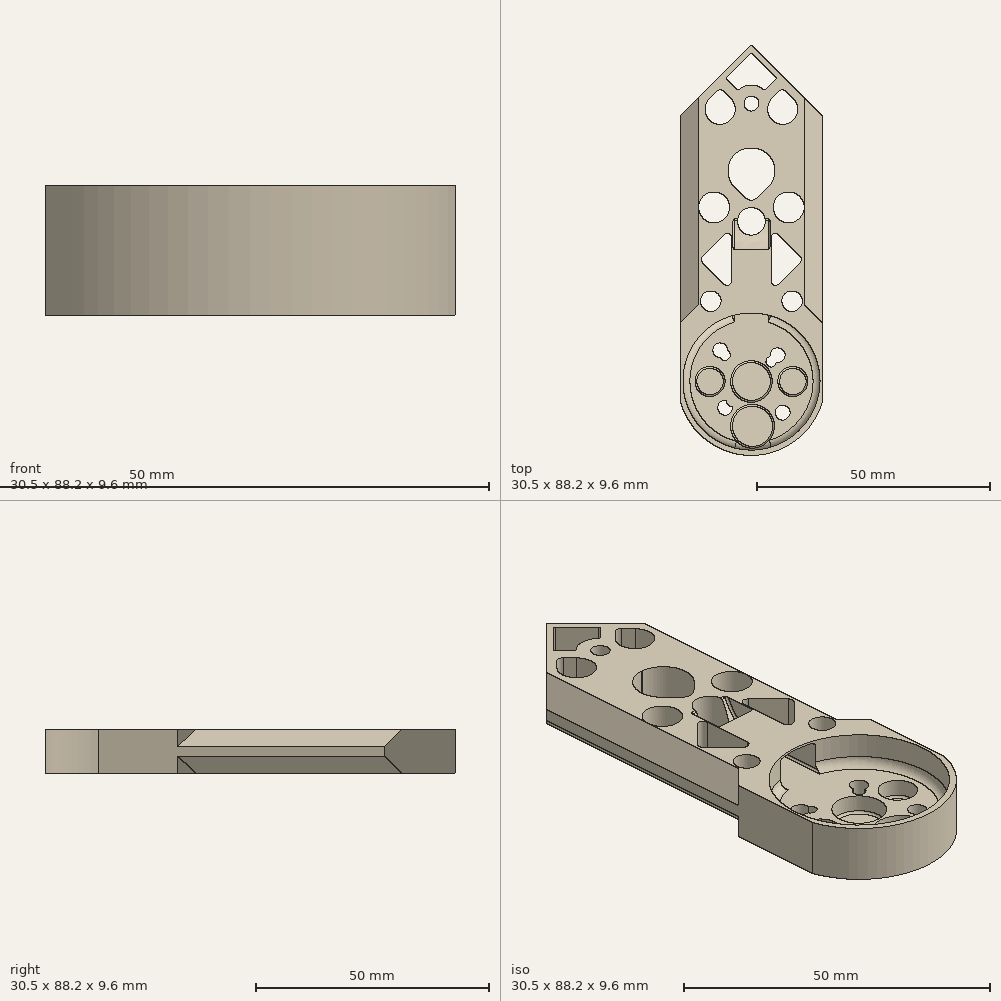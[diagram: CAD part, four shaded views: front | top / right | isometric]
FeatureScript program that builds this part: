
annotation { "Feature Type Name" : "Feature", "Feature Type Description" : "" }
export const myFeature = defineFeature(function(context is Context, id is Id, definition is map)
    precondition{}
    {
        {
            var Q0;
            Q0=qCreatedBy(makeId("Top.planeOp"),FACE);
            var sketch = newSketch(context, id + "F0", { "sketchPlane" : qUnion([Q0])});
            skLineSegment(sketch, "E0", {"start": v(0, 0) * mm, "end": v(-10, 0) * mm});
            skLineSegment(sketch, "E1", {"start": v(-7.84, 7.84) * mm, "end": v(0, 0) * mm});
            skLineSegment(sketch, "E2", {"start": v(-6.78, -6.78) * mm, "end": v(0, 0) * mm});
            skLineSegment(sketch, "E3", {"start": v(0, 0) * mm, "end": v(-5.66, -5.66) * mm});
            skCircle(sketch, "E4", {"center": v(-5.66, -5.66) * mm, "radius": 1.59 * mm});
            skLineSegment(sketch, "E5", {"start": v(0, 0) * mm, "end": v(-6.72, 6.72) * mm});
            skCircle(sketch, "E6", {"center": v(-6.72, 6.72) * mm, "radius": 1.59 * mm});
            skLineSegment(sketch, "E7", {"start": v(0, 0) * mm, "end": v(-5.66, 5.66) * mm});
            skCircle(sketch, "E8", {"center": v(-5.66, 5.66) * mm, "radius": 1.13 * mm});
            skLineSegment(sketch, "E9.MirrorCS", {"start": v(7.84, -7.84) * mm, "end": v(0, 0) * mm});
            skLineSegment(sketch, "E10.MirrorCS", {"start": v(0, 0) * mm, "end": v(5.66, -5.66) * mm});
            skCircle(sketch, "E11.MirrorC", {"center": v(6.72, -6.72) * mm, "radius": 1.59 * mm});
            skCircle(sketch, "E12.MirrorC", {"center": v(5.66, -5.66) * mm, "radius": 1.13 * mm});
            skLineSegment(sketch, "E13.MirrorCS", {"start": v(0, 0) * mm, "end": v(6.72, -6.72) * mm});
            skCircle(sketch, "E14.MirrorC", {"center": v(5.66, 5.66) * mm, "radius": 1.59 * mm});
            skLineSegment(sketch, "E15.MirrorCS", {"start": v(0, 0) * mm, "end": v(5.66, 5.66) * mm});
            skLineSegment(sketch, "E16.MirrorCS", {"start": v(6.78, 6.78) * mm, "end": v(0, 0) * mm});
            skPoint(sketch, "E17.MirrorCS.start.orphan", {"position": v(0, 10) * mm});
            skPoint(sketch, "E18.orphan", {"position": v(10, 10) * mm});
            skPoint(sketch, "E19.orphan", {"position": v(10, -10) * mm});
            skPoint(sketch, "E20.orphan", {"position": v(-10, 10) * mm});
            skPoint(sketch, "E21.orphan", {"position": v(-10, -10) * mm});
            skCircle(sketch, "E22", {"center": v(-4.24, -4.24) * mm, "radius": 1.13 * mm});
            skCircle(sketch, "E23", {"center": v(4.24, 4.24) * mm, "radius": 1.13 * mm});
            skSolve(sketch);
        }
        {
            var Q0;
            Q0=qCreatedBy(makeId("Front.planeOp"),FACE);
            var sketch = newSketch(context, id + "F1", { "sketchPlane" : qUnion([Q0])});
            skLineSegment(sketch, "E24", {"start": v(0, 0) * mm, "end": v(11.35, 0) * mm});
            skLineSegment(sketch, "E25", {"start": v(-11.35, 0) * mm, "end": v(0, 0) * mm});
            skLineSegment(sketch, "E26", {"start": v(0, 0) * mm, "end": v(0, 3.8) * mm});
            skLineSegment(sketch, "E27", {"start": v(0, 3.8) * mm, "end": v(15.25, 3.8) * mm});
            skLineSegment(sketch, "E28", {"start": v(-15.25, 3.8) * mm, "end": v(0, 3.8) * mm});
            skPoint(sketch, "E29.orphan", {"position": v(15.25, 0) * mm});
            skPoint(sketch, "E30.orphan", {"position": v(-15.25, 0) * mm});
            skLineSegment(sketch, "E31", {"start": v(-15.25, 3.8) * mm, "end": v(-11.35, 0) * mm});
            skLineSegment(sketch, "E32", {"start": v(15.25, 3.8) * mm, "end": v(11.35, 0) * mm});
            skLineSegment(sketch, "E33", {"start": v(15.25, 3.8) * mm, "end": v(15.25, 5.8) * mm});
            skLineSegment(sketch, "E34", {"start": v(15.25, 5.8) * mm, "end": v(11.35, 9.6) * mm});
            skLineSegment(sketch, "E35", {"start": v(11.35, 9.6) * mm, "end": v(0, 9.6) * mm});
            skLineSegment(sketch, "E36.MirrorCS", {"start": v(-11.35, 9.6) * mm, "end": v(0, 9.6) * mm});
            skLineSegment(sketch, "E37.MirrorCS", {"start": v(-15.25, 5.8) * mm, "end": v(-11.35, 9.6) * mm});
            skLineSegment(sketch, "E38.MirrorCS", {"start": v(-15.25, 3.8) * mm, "end": v(-15.25, 5.8) * mm});
            skSolve(sketch);
        }
        {
            var Q0;
            Q0=qSketchRegion(id+"F1",true);
            extrude(context, id + "F2", {"entities" : qUnion([Q0]), "depth" : 16.3 * mm, "hasSecondDirection" : true, "secondDirectionOppositeDirection" : true, "secondDirectionDepth" : 72.3 * mm});
        }
        {
            var Q0;
            Q0=qCreatedBy(makeId("Top.planeOp"),FACE);
            cPlane(context, id + "F3", {"entities" : qUnion([Q0]), "cplaneType" : CPlaneType.OFFSET, "offset" : 16 * mm, "width" : 150 * mm, "height" : 150 * mm});
        }
        {
            var Q0;
            Q0=makeQuery(id+"F2.opExtrude","SWEPT_FACE",FACE,{"disambiguationData":[OSD([sQuery(id+"F1.wireOp",EDGE,"E35"),sQuery(id+"F1.wireOp",EDGE,"E36.MirrorCS")])]});
            var sketch = newSketch(context, id + "F4", { "sketchPlane" : qUnion([Q0])});
            skCircle(sketch, "E39", {"center": v(0, 0) * mm, "radius": 14.75 * mm});
            skLineSegment(sketch, "E40", {"start": v(14.75, 0) * mm, "end": v(-14.75, 0) * mm});
            skSolve(sketch);
        }
        {
            var Q0;
            {var subQ0=sQuery(id+"F4.wireOp",EDGE,"E39");var subQ1=makeQuery(id+"F2.opExtrude","SWEPT_EDGE",EDGE,{"disambiguationData":[OSD([sQuery(id+"F1.wireOp",EDGE,"E34"),sQuery(id+"F1.wireOp",EDGE,"E35")])]});var subQ2=makeQuery(id+"F4.imprint","INTERSECT",VERTEX,{"disambiguationData":[OD(0.0)],"derivedFrom":[subQ1,subQ0]});Q0=makeQuery(id+"F4.imprint","IMPRINT",FACE,{"disambiguationData":[TD([[makeQuery(id+"F4.imprint","IMPRINT",EDGE,{"disambiguationData":[TD([[subQ2,-1.0]])],"derivedFrom":subQ0}),1.0]])]});}
            var Q1;
            {var subQ0=sQuery(id+"F4.wireOp",EDGE,"E39");var subQ1=makeQuery(id+"F2.opExtrude","SWEPT_EDGE",EDGE,{"disambiguationData":[OSD([sQuery(id+"F1.wireOp",EDGE,"E36.MirrorCS"),sQuery(id+"F1.wireOp",EDGE,"E37.MirrorCS")])]});var subQ2=makeQuery(id+"F4.imprint","INTERSECT",VERTEX,{"disambiguationData":[OD(1.0)],"derivedFrom":[subQ1,subQ0]});Q1=makeQuery(id+"F4.imprint","IMPRINT",FACE,{"disambiguationData":[TD([[makeQuery(id+"F4.imprint","IMPRINT",EDGE,{"disambiguationData":[TD([[subQ2,-1.0]])],"derivedFrom":subQ0}),1.0]])]});}
            var Q2;
            {var subQ0=sQuery(id+"F4.wireOp",EDGE,"E40");var subQ1=sQuery(id+"F4.wireOp",EDGE,"E39");var subQ2=makeQuery(id+"F4.imprint","INTERSECT",VERTEX,{"disambiguationData":[OD(1.0)],"derivedFrom":[subQ1,subQ0]});Q2=makeQuery(id+"F4.imprint","IMPRINT",FACE,{"disambiguationData":[TD([[makeQuery(id+"F4.imprint","IMPRINT",EDGE,{"disambiguationData":[TD([[subQ2,-1.0]])],"derivedFrom":subQ1}),1.0]])]});}
            var Q3;
            {var subQ0=sQuery(id+"F4.wireOp",EDGE,"E40");var subQ1=sQuery(id+"F4.wireOp",EDGE,"E39");var subQ2=makeQuery(id+"F4.imprint","INTERSECT",VERTEX,{"disambiguationData":[OD(1.0)],"derivedFrom":[subQ1,subQ0]});Q3=makeQuery(id+"F4.imprint","IMPRINT",FACE,{"disambiguationData":[TD([[makeQuery(id+"F4.imprint","IMPRINT",EDGE,{"disambiguationData":[TD([[subQ2,1.0]])],"derivedFrom":subQ1}),1.0]])]});}
            var Q4;
            {var subQ0=sQuery(id+"F4.wireOp",EDGE,"E40");var subQ1=sQuery(id+"F4.wireOp",EDGE,"E39");var subQ2=makeQuery(id+"F4.imprint","INTERSECT",VERTEX,{"disambiguationData":[OD(0.0)],"derivedFrom":[subQ1,subQ0]});Q4=makeQuery(id+"F4.imprint","IMPRINT",FACE,{"disambiguationData":[TD([[makeQuery(id+"F4.imprint","IMPRINT",EDGE,{"disambiguationData":[TD([[subQ2,-1.0]])],"derivedFrom":subQ1}),1.0]])]});}
            var Q5;
            {var subQ0=sQuery(id+"F4.wireOp",EDGE,"E40");var subQ1=sQuery(id+"F4.wireOp",EDGE,"E39");var subQ2=makeQuery(id+"F4.imprint","INTERSECT",VERTEX,{"disambiguationData":[OD(0.0)],"derivedFrom":[subQ1,subQ0]});Q5=makeQuery(id+"F4.imprint","IMPRINT",FACE,{"disambiguationData":[TD([[makeQuery(id+"F4.imprint","IMPRINT",EDGE,{"disambiguationData":[TD([[subQ2,1.0]])],"derivedFrom":subQ1}),1.0]])]});}
            extrude(context, id + "F5", {"entities" : qUnion([Q0, Q1, Q2, Q3, Q4, Q5]), "operationType" : NewBodyOperationType.REMOVE, "oppositeDirection" : true, "depth" : 5.6 * mm});
        }
        {
            var Q0;
            {var subQ5=sQuery(id+"F0.wireOp",EDGE,"E1");Q0=makeQuery(id+"F0.imprint","IMPRINT",FACE,{"disambiguationData":[TD([[makeQuery(id+"F0.imprint","IMPRINT",EDGE,{"derivedFrom":subQ5}),-1.0]])]});}
            var Q1;
            {var subQ3=sQuery(id+"F0.wireOp",EDGE,"E1");Q1=makeQuery(id+"F0.imprint","IMPRINT",FACE,{"disambiguationData":[TD([[makeQuery(id+"F0.imprint","IMPRINT",EDGE,{"derivedFrom":subQ3}),1.0]])]});}
            var Q2;
            {var subQ5=sQuery(id+"F0.wireOp",EDGE,"E2");Q2=makeQuery(id+"F0.imprint","IMPRINT",FACE,{"disambiguationData":[TD([[makeQuery(id+"F0.imprint","IMPRINT",EDGE,{"derivedFrom":subQ5}),1.0]])]});}
            var Q3;
            {var subQ5=sQuery(id+"F0.wireOp",EDGE,"E2");Q3=makeQuery(id+"F0.imprint","IMPRINT",FACE,{"disambiguationData":[TD([[makeQuery(id+"F0.imprint","IMPRINT",EDGE,{"derivedFrom":subQ5}),-1.0]])]});}
            var Q4;
            {var subQ0=sQuery(id+"F0.wireOp",EDGE,"E22");var subQ3=sQuery(id+"F0.wireOp",EDGE,"E3");var subQ4=makeQuery(id+"F0.imprint","INTERSECT",VERTEX,{"disambiguationData":[OD(0.0)],"derivedFrom":[subQ3,subQ0]});Q4=makeQuery(id+"F0.imprint","IMPRINT",FACE,{"disambiguationData":[TD([[makeQuery(id+"F0.imprint","IMPRINT",EDGE,{"disambiguationData":[TD([[subQ4,-1.0]])],"derivedFrom":subQ3}),1.0]])]});}
            var Q5;
            {var subQ0=sQuery(id+"F0.wireOp",EDGE,"E22");var subQ3=sQuery(id+"F0.wireOp",EDGE,"E3");var subQ4=makeQuery(id+"F0.imprint","INTERSECT",VERTEX,{"disambiguationData":[OD(0.0)],"derivedFrom":[subQ3,subQ0]});Q5=makeQuery(id+"F0.imprint","IMPRINT",FACE,{"disambiguationData":[TD([[makeQuery(id+"F0.imprint","IMPRINT",EDGE,{"disambiguationData":[TD([[subQ4,-1.0]])],"derivedFrom":subQ3}),-1.0]])]});}
            var Q6;
            {var subQ1=sQuery(id+"F0.wireOp",EDGE,"E6");var subQ3=sQuery(id+"F0.wireOp",EDGE,"E8");var subQ5=makeQuery(id+"F0.imprint","INTERSECT",VERTEX,{"disambiguationData":[OD(0.0)],"derivedFrom":[subQ1,subQ3]});Q6=makeQuery(id+"F0.imprint","IMPRINT",FACE,{"disambiguationData":[TD([[makeQuery(id+"F0.imprint","IMPRINT",EDGE,{"disambiguationData":[TD([[subQ5,-1.0]])],"derivedFrom":subQ1}),-1.0]])]});}
            var Q7;
            {var subQ1=sQuery(id+"F0.wireOp",EDGE,"E6");var subQ3=sQuery(id+"F0.wireOp",EDGE,"E8");var subQ5=makeQuery(id+"F0.imprint","INTERSECT",VERTEX,{"disambiguationData":[OD(1.0)],"derivedFrom":[subQ1,subQ3]});Q7=makeQuery(id+"F0.imprint","IMPRINT",FACE,{"disambiguationData":[TD([[makeQuery(id+"F0.imprint","IMPRINT",EDGE,{"disambiguationData":[TD([[subQ5,1.0]])],"derivedFrom":subQ1}),-1.0]])]});}
            var Q8;
            {var subQ3=sQuery(id+"F0.wireOp",EDGE,"E9.MirrorCS");Q8=makeQuery(id+"F0.imprint","IMPRINT",FACE,{"disambiguationData":[TD([[makeQuery(id+"F0.imprint","IMPRINT",EDGE,{"derivedFrom":subQ3}),1.0]])]});}
            var Q9;
            {var subQ3=sQuery(id+"F0.wireOp",EDGE,"E9.MirrorCS");Q9=makeQuery(id+"F0.imprint","IMPRINT",FACE,{"disambiguationData":[TD([[makeQuery(id+"F0.imprint","IMPRINT",EDGE,{"derivedFrom":subQ3}),-1.0]])]});}
            var Q10;
            {var subQ1=sQuery(id+"F0.wireOp",EDGE,"E11.MirrorC");var subQ3=sQuery(id+"F0.wireOp",EDGE,"E12.MirrorC");var subQ5=makeQuery(id+"F0.imprint","INTERSECT",VERTEX,{"disambiguationData":[OD(0.0)],"derivedFrom":[subQ1,subQ3]});Q10=makeQuery(id+"F0.imprint","IMPRINT",FACE,{"disambiguationData":[TD([[makeQuery(id+"F0.imprint","IMPRINT",EDGE,{"disambiguationData":[TD([[subQ5,-1.0]])],"derivedFrom":subQ1}),1.0]])]});}
            var Q11;
            {var subQ1=sQuery(id+"F0.wireOp",EDGE,"E11.MirrorC");var subQ3=sQuery(id+"F0.wireOp",EDGE,"E12.MirrorC");var subQ5=makeQuery(id+"F0.imprint","INTERSECT",VERTEX,{"disambiguationData":[OD(1.0)],"derivedFrom":[subQ1,subQ3]});Q11=makeQuery(id+"F0.imprint","IMPRINT",FACE,{"disambiguationData":[TD([[makeQuery(id+"F0.imprint","IMPRINT",EDGE,{"disambiguationData":[TD([[subQ5,1.0]])],"derivedFrom":subQ1}),1.0]])]});}
            var Q12;
            {var subQ0=sQuery(id+"F0.wireOp",EDGE,"E23");var subQ1=sQuery(id+"F0.wireOp",EDGE,"E14.MirrorC");var subQ2=makeQuery(id+"F0.imprint","INTERSECT",VERTEX,{"disambiguationData":[OD(1.0)],"derivedFrom":[subQ1,subQ0]});Q12=makeQuery(id+"F0.imprint","IMPRINT",FACE,{"disambiguationData":[TD([[makeQuery(id+"F0.imprint","IMPRINT",EDGE,{"disambiguationData":[TD([[subQ2,1.0]])],"derivedFrom":subQ1}),1.0]])]});}
            var Q13;
            {var subQ1=sQuery(id+"F0.wireOp",EDGE,"E16.MirrorCS");var subQ5=makeQuery(id+"F0.imprint","IMPRINT",VERTEX,{"derivedFrom":subQ1});Q13=makeQuery(id+"F0.imprint","IMPRINT",FACE,{"disambiguationData":[TD([[makeQuery(id+"F0.imprint","IMPRINT",EDGE,{"disambiguationData":[TD([[subQ5,1.0]])],"derivedFrom":subQ1}),-1.0]])]});}
            var Q14;
            {var subQ1=sQuery(id+"F0.wireOp",EDGE,"E16.MirrorCS");var subQ5=makeQuery(id+"F0.imprint","IMPRINT",VERTEX,{"derivedFrom":subQ1});Q14=makeQuery(id+"F0.imprint","IMPRINT",FACE,{"disambiguationData":[TD([[makeQuery(id+"F0.imprint","IMPRINT",EDGE,{"disambiguationData":[TD([[subQ5,1.0]])],"derivedFrom":subQ1}),1.0]])]});}
            var Q15;
            {var subQ1=sQuery(id+"F0.wireOp",EDGE,"E3");var subQ3=sQuery(id+"F0.wireOp",EDGE,"E4");var subQ5=makeQuery(id+"F0.imprint","INTERSECT",VERTEX,{"derivedFrom":[subQ1,subQ3]});Q15=makeQuery(id+"F0.imprint","IMPRINT",FACE,{"disambiguationData":[TD([[makeQuery(id+"F0.imprint","IMPRINT",EDGE,{"disambiguationData":[TD([[subQ5,-1.0]])],"derivedFrom":subQ1}),1.0]])]});}
            var Q16;
            {var subQ1=sQuery(id+"F0.wireOp",EDGE,"E3");var subQ3=sQuery(id+"F0.wireOp",EDGE,"E4");var subQ5=makeQuery(id+"F0.imprint","INTERSECT",VERTEX,{"derivedFrom":[subQ1,subQ3]});Q16=makeQuery(id+"F0.imprint","IMPRINT",FACE,{"disambiguationData":[TD([[makeQuery(id+"F0.imprint","IMPRINT",EDGE,{"disambiguationData":[TD([[subQ5,-1.0]])],"derivedFrom":subQ1}),-1.0]])]});}
            var Q17;
            {var subQ0=sQuery(id+"F0.wireOp",EDGE,"E13.MirrorCS");var subQ3=makeQuery(id+"F0.imprint","IMPRINT",VERTEX,{"derivedFrom":subQ0});Q17=makeQuery(id+"F0.imprint","IMPRINT",FACE,{"disambiguationData":[TD([[makeQuery(id+"F0.imprint","IMPRINT",EDGE,{"disambiguationData":[TD([[subQ3,1.0]])],"derivedFrom":subQ0}),1.0]])]});}
            var Q18;
            {var subQ0=sQuery(id+"F0.wireOp",EDGE,"E23");var subQ3=sQuery(id+"F0.wireOp",EDGE,"E14.MirrorC");var subQ4=makeQuery(id+"F0.imprint","INTERSECT",VERTEX,{"disambiguationData":[OD(1.0)],"derivedFrom":[subQ3,subQ0]});Q18=makeQuery(id+"F0.imprint","IMPRINT",FACE,{"disambiguationData":[TD([[makeQuery(id+"F0.imprint","IMPRINT",EDGE,{"disambiguationData":[TD([[subQ4,1.0]])],"derivedFrom":subQ3}),-1.0]])]});}
            var Q19;
            {var subQ0=sQuery(id+"F0.wireOp",EDGE,"E23");var subQ1=sQuery(id+"F0.wireOp",EDGE,"E14.MirrorC");var subQ2=makeQuery(id+"F0.imprint","INTERSECT",VERTEX,{"disambiguationData":[OD(0.0)],"derivedFrom":[subQ1,subQ0]});Q19=makeQuery(id+"F0.imprint","IMPRINT",FACE,{"disambiguationData":[TD([[makeQuery(id+"F0.imprint","IMPRINT",EDGE,{"disambiguationData":[TD([[subQ2,-1.0]])],"derivedFrom":subQ1}),1.0]])]});}
            var Q20;
            {var subQ0=sQuery(id+"F0.wireOp",EDGE,"E23");var subQ3=sQuery(id+"F0.wireOp",EDGE,"E14.MirrorC");var subQ4=makeQuery(id+"F0.imprint","INTERSECT",VERTEX,{"disambiguationData":[OD(0.0)],"derivedFrom":[subQ3,subQ0]});Q20=makeQuery(id+"F0.imprint","IMPRINT",FACE,{"disambiguationData":[TD([[makeQuery(id+"F0.imprint","IMPRINT",EDGE,{"disambiguationData":[TD([[subQ4,-1.0]])],"derivedFrom":subQ3}),-1.0]])]});}
            var Q21;
            {var subQ0=sQuery(id+"F0.wireOp",EDGE,"E13.MirrorCS");var subQ3=makeQuery(id+"F0.imprint","IMPRINT",VERTEX,{"derivedFrom":subQ0});Q21=makeQuery(id+"F0.imprint","IMPRINT",FACE,{"disambiguationData":[TD([[makeQuery(id+"F0.imprint","IMPRINT",EDGE,{"disambiguationData":[TD([[subQ3,1.0]])],"derivedFrom":subQ0}),-1.0]])]});}
            var Q22;
            {var subQ1=sQuery(id+"F0.wireOp",EDGE,"E5");var subQ5=sQuery(id+"F0.wireOp",EDGE,"E7");var subQ7=makeQuery(id+"F0.imprint","INTERSECT",VERTEX,{"derivedFrom":[subQ1,subQ5]});Q22=makeQuery(id+"F0.imprint","IMPRINT",FACE,{"disambiguationData":[TD([[makeQuery(id+"F0.imprint","IMPRINT",EDGE,{"disambiguationData":[TD([[subQ7,-1.0]])],"derivedFrom":subQ1}),1.0]])]});}
            var Q23;
            {var subQ1=sQuery(id+"F0.wireOp",EDGE,"E5");var subQ5=sQuery(id+"F0.wireOp",EDGE,"E7");var subQ7=makeQuery(id+"F0.imprint","INTERSECT",VERTEX,{"derivedFrom":[subQ1,subQ5]});Q23=makeQuery(id+"F0.imprint","IMPRINT",FACE,{"disambiguationData":[TD([[makeQuery(id+"F0.imprint","IMPRINT",EDGE,{"disambiguationData":[TD([[subQ7,-1.0]])],"derivedFrom":subQ1}),-1.0]])]});}
            extrude(context, id + "F6", {"entities" : qUnion([Q0, Q1, Q2, Q3, Q4, Q5, Q6, Q7, Q8, Q9, Q10, Q11, Q12, Q13, Q14, Q15, Q16, Q17, Q18, Q19, Q20, Q21, Q22, Q23]), "operationType" : NewBodyOperationType.REMOVE, "endBound" : BoundingType.THROUGH_ALL, "depth" : 5 * mm});
        }
        {
            var Q0;
            Q0=qCreatedBy(makeId("Top.planeOp"),FACE);
            var sketch = newSketch(context, id + "F7", { "sketchPlane" : qUnion([Q0])});
            skCircle(sketch, "E41", {"center": v(0, 0) * mm, "radius": 14.75 * mm});
            skArc(sketch, "E42", {"start": v(15.25, 4.5) * mm, "mid": v(0, 15.9) * mm, "end": v(-15.25, 4.5) * mm});
            skLineSegment(sketch, "E43", {"start": v(0, 0) * mm, "end": v(15.25, 0) * mm});
            skLineSegment(sketch, "E44", {"start": v(15.25, 0) * mm, "end": v(15.25, 4.5) * mm});
            skLineSegment(sketch, "E45.MirrorCS", {"start": v(15.25, 0) * mm, "end": v(15.25, -4.5) * mm});
            skLineSegment(sketch, "E46.MirrorCS", {"start": v(-15.25, 0) * mm, "end": v(-15.25, 4.5) * mm});
            skLineSegment(sketch, "E47.MirrorCS", {"start": v(-15.25, 0) * mm, "end": v(-15.25, -4.5) * mm});
            skArc(sketch, "E48.trimOffspring", {"start": v(-15.25, -4.5) * mm, "mid": v(0, -15.9) * mm, "end": v(15.25, -4.5) * mm});
            skSolve(sketch);
        }
        {
            var Q0;
            Q0=qSketchRegion(id+"F7",true);
            var Q1;
            Q1=makeQuery(id+"F2.opExtrude","SWEPT_FACE",FACE,{"disambiguationData":[OSD([sQuery(id+"F1.wireOp",EDGE,"E35"),sQuery(id+"F1.wireOp",EDGE,"E36.MirrorCS")])]});
            extrude(context, id + "F8", {"entities" : qUnion([Q0]), "operationType" : NewBodyOperationType.ADD, "endBound" : BoundingType.UP_TO_SURFACE, "endBoundEntityFace" : qUnion([Q1]), "depth" : 15.75 * mm});
        }
        {
            var Q0;
            Q0=qCreatedBy(id+"F3.planeOp",FACE);
            var sketch = newSketch(context, id + "F9", { "sketchPlane" : qUnion([Q0])});
            skCircle(sketch, "E49", {"center": v(0, 0) * mm, "radius": 15.9 * mm});
            skLineSegment(sketch, "E50", {"start": v(-15.9, 0) * mm, "end": v(-15.9, -16.3) * mm});
            skLineSegment(sketch, "E51.bottom", {"start": v(-15.9, -16.3) * mm, "end": v(15.9, -16.3) * mm});
            skLineSegment(sketch, "E51.top", {"start": v(-15.9, 0) * mm, "end": v(15.9, 0) * mm});
            skLineSegment(sketch, "E51.left", {"start": v(-15.9, -16.3) * mm, "end": v(-15.9, 0) * mm});
            skLineSegment(sketch, "E51.right", {"start": v(15.9, -16.3) * mm, "end": v(15.9, 0) * mm});
            skLineSegment(sketch, "E52", {"start": v(0, 0) * mm, "end": v(-3.75, 0) * mm});
            skLineSegment(sketch, "E53.bottom", {"start": v(-3.75, -16.3) * mm, "end": v(3.75, -16.3) * mm});
            skSolve(sketch);
        }
        {
            var Q0;
            {var subQ3=sQuery(id+"F9.wireOp",EDGE,"E51.left");Q0=makeQuery(id+"F9.imprint","IMPRINT",FACE,{"disambiguationData":[TD([[makeQuery(id+"F9.imprint","IMPRINT",EDGE,{"derivedFrom":subQ3}),-1.0]])]});}
            var Q1;
            {var subQ3=sQuery(id+"F9.wireOp",EDGE,"E51.left");Q1=makeQuery(id+"F9.imprint","IMPRINT",FACE,{"disambiguationData":[TD([[makeQuery(id+"F9.imprint","IMPRINT",EDGE,{"derivedFrom":subQ3}),-1.0]])]});}
            var Q2;
            {var subQ0=sQuery(id+"F9.wireOp",EDGE,"E51.right");Q2=makeQuery(id+"F9.imprint","IMPRINT",FACE,{"disambiguationData":[TD([[makeQuery(id+"F9.imprint","IMPRINT",EDGE,{"derivedFrom":subQ0}),1.0]])]});}
            extrude(context, id + "F10", {"entities" : qUnion([Q0, Q1, Q2]), "operationType" : NewBodyOperationType.REMOVE, "oppositeDirection" : true, "depth" : 25 * mm});
        }
        {
            var Q0;
            Q0=makeQuery(id+"F5.boolean.opBoolean","COPY",FACE,{"derivedFrom":makeQuery(id+"F5.opExtrude","CAP_FACE",FACE,{"disambiguationData":[OSD([sQuery(id+"F4.wireOp",EDGE,"E39")])],"isStart":false})});
            var sketch = newSketch(context, id + "F11", { "sketchPlane" : qUnion([Q0])});
            skCircle(sketch, "E54", {"center": v(0, 0) * mm, "radius": 4.47 * mm});
            skLineSegment(sketch, "E55", {"start": v(0, 0) * mm, "end": v(8.91, 0) * mm});
            skCircle(sketch, "E56", {"center": v(0.24, -9.63) * mm, "radius": 4.72 * mm});
            skLineSegment(sketch, "E57.MirrorCS", {"start": v(0, 0) * mm, "end": v(-8.91, 0) * mm});
            skCircle(sketch, "E58", {"center": v(8.91, 0) * mm, "radius": 3.24 * mm});
            skCircle(sketch, "E59.MirrorC", {"center": v(-8.91, 0) * mm, "radius": 3.24 * mm});
            skSolve(sketch);
        }
        {
            var Q0;
            Q0=qSketchRegion(id+"F11",true);
            extrude(context, id + "F12", {"entities" : qUnion([Q0]), "operationType" : NewBodyOperationType.REMOVE, "oppositeDirection" : true, "depth" : 3.2 * mm});
        }
        {
            var Q0;
            Q0=qCreatedBy(makeId("Top.planeOp"),FACE);
            cPlane(context, id + "F13", {"entities" : qUnion([Q0]), "cplaneType" : CPlaneType.OFFSET, "offset" : 0 * mm, "width" : 150 * mm, "height" : 150 * mm});
        }
        {
            var Q0;
            Q0=qCreatedBy(makeId("Top.planeOp"),FACE);
            var sketch = newSketch(context, id + "F14", { "sketchPlane" : qUnion([Q0])});
            skLineSegment(sketch, "E60", {"start": v(0, 57.05) * mm, "end": v(15.25, 57.05) * mm});
            skLineSegment(sketch, "E61", {"start": v(15.25, 57.05) * mm, "end": v(0, 72.3) * mm});
            skLineSegment(sketch, "E62.MirrorCS", {"start": v(-15.25, 57.05) * mm, "end": v(0, 72.3) * mm});
            skLineSegment(sketch, "E63.MirrorCS", {"start": v(0, 57.05) * mm, "end": v(-15.25, 57.05) * mm});
            skLineSegment(sketch, "E64", {"start": v(-15.25, 57.05) * mm, "end": v(-15.25, 72.3) * mm});
            skLineSegment(sketch, "E65", {"start": v(-15.25, 72.3) * mm, "end": v(15.25, 72.3) * mm});
            skLineSegment(sketch, "E66", {"start": v(15.25, 72.3) * mm, "end": v(15.25, 57.05) * mm});
            skSolve(sketch);
        }
        {
            var Q0;
            Q0=makeQuery(id+"F14.imprint","IMPRINT",FACE,{"disambiguationData":[TD([[makeQuery(id+"F14.imprint","IMPRINT",EDGE,{"derivedFrom":sQuery(id+"F14.wireOp",EDGE,"E61")}),-1.0]])]});
            var Q1;
            {var subQ0=sQuery(id+"F14.wireOp",EDGE,"E62.MirrorCS");Q1=makeQuery(id+"F14.imprint","IMPRINT",FACE,{"disambiguationData":[TD([[makeQuery(id+"F14.imprint","IMPRINT",EDGE,{"derivedFrom":subQ0}),1.0]])]});}
            extrude(context, id + "F15", {"entities" : qUnion([Q0, Q1]), "operationType" : NewBodyOperationType.REMOVE, "depth" : 25 * mm});
        }
        {
            var Q0;
            {var subQ0=sQuery(id+"F1.wireOp",EDGE,"E38.MirrorCS");var subQ1=sQuery(id+"F1.wireOp",EDGE,"E37.MirrorCS");var subQ2=sQuery(id+"F1.wireOp",EDGE,"E36.MirrorCS");var subQ3=sQuery(id+"F1.wireOp",EDGE,"E35");var subQ4=sQuery(id+"F1.wireOp",EDGE,"E34");var subQ5=sQuery(id+"F1.wireOp",EDGE,"E33");var subQ6=sQuery(id+"F1.wireOp",EDGE,"E32");var subQ7=sQuery(id+"F1.wireOp",EDGE,"E31");var subQ8=sQuery(id+"F1.wireOp",EDGE,"E25");var subQ9=sQuery(id+"F1.wireOp",EDGE,"E24");var subQ13=makeQuery(id+"F2.opExtrude","SWEPT_FACE",FACE,{"disambiguationData":[OSD([subQ3,subQ2])]});Q0=makeQuery(id+"F8.boolean.opBoolean","MERGE",FACE,{"derivedFrom":[makeQuery(id+"F5.boolean.opBoolean","SPLIT",FACE,{"disambiguationData":[TD([makeQuery(id+"F2.opExtrude","CAP_FACE",FACE,{"disambiguationData":[OSD([subQ9,subQ8,subQ7,subQ6,subQ5,subQ4,subQ3,subQ2,subQ1,subQ0])],"isStart":true})])],"derivedFrom":subQ13}),makeQuery(id+"F5.boolean.opBoolean","SPLIT",FACE,{"disambiguationData":[TD([makeQuery(id+"F2.opExtrude","CAP_FACE",FACE,{"disambiguationData":[OSD([subQ9,subQ8,subQ7,subQ6,subQ5,subQ4,subQ3,subQ2,subQ1,subQ0])],"isStart":false})])],"derivedFrom":subQ13}),makeQuery(id+"F8.opExtrude","CAP_FACE",FACE,{"disambiguationData":[OSD([sQuery(id+"F7.wireOp",EDGE,"E41"),sQuery(id+"F7.wireOp",EDGE,"E42")])],"isStart":false})]});}
            var sketch = newSketch(context, id + "F16", { "sketchPlane" : qUnion([Q0])});
            skLineSegment(sketch, "E67", {"start": v(0, 72.3) * mm, "end": v(0, 59.8) * mm});
            skCircle(sketch, "E68", {"center": v(0, 59.8) * mm, "radius": 1.6 * mm});
            skLineSegment(sketch, "E69.0", {"start": v(5.2, 65.5) * mm, "end": v(0.28, 70.42) * mm});
            skLineSegment(sketch, "E69.1", {"start": v(-5.23, 65.47) * mm, "end": v(-0.28, 70.42) * mm});
            skPoint(sketch, "E70.visualSharp", {"position": v(0, 70.7) * mm});
            skArc(sketch, "E70.filletArc", {"start": v(0.28, 70.42) * mm, "mid": v(0, 70.53) * mm, "end": v(-0.28, 70.42) * mm});
            skArc(sketch, "E71", {"start": v(2.58, 62.85) * mm, "mid": v(-0.02, 63.8) * mm, "end": v(-2.62, 62.82) * mm});
            skLineSegment(sketch, "E72.trimOffspring", {"start": v(-3.16, 62.84) * mm, "end": v(-5.23, 64.9) * mm});
            skLineSegment(sketch, "E73.trimOffspring", {"start": v(3.12, 62.88) * mm, "end": v(5.2, 64.94) * mm});
            skPoint(sketch, "E74.visualSharp", {"position": v(-5.51, 65.19) * mm});
            skArc(sketch, "E74.filletArc", {"start": v(-5.23, 65.47) * mm, "mid": v(-5.35, 65.19) * mm, "end": v(-5.23, 64.9) * mm});
            skPoint(sketch, "E75.visualSharp", {"position": v(5.47, 65.23) * mm});
            skArc(sketch, "E75.filletArc", {"start": v(5.2, 64.94) * mm, "mid": v(5.3, 65.23) * mm, "end": v(5.2, 65.5) * mm});
            skPoint(sketch, "E76.visualSharp", {"position": v(-2.89, 62.57) * mm});
            skArc(sketch, "E76.filletArc", {"start": v(-3.16, 62.84) * mm, "mid": v(-2.9, 62.73) * mm, "end": v(-2.62, 62.82) * mm});
            skPoint(sketch, "E77.visualSharp", {"position": v(2.85, 62.6) * mm});
            skArc(sketch, "E77.filletArc", {"start": v(2.58, 62.85) * mm, "mid": v(2.86, 62.76) * mm, "end": v(3.12, 62.88) * mm});
            skSolve(sketch);
        }
        {
            var Q0;
            {var subQ4=sQuery(id+"F16.wireOp",EDGE,"E69.0");Q0=makeQuery(id+"F16.imprint","IMPRINT",FACE,{"disambiguationData":[TD([[makeQuery(id+"F16.imprint","IMPRINT",EDGE,{"derivedFrom":subQ4}),1.0]])]});}
            var Q1;
            {var subQ4=sQuery(id+"F16.wireOp",EDGE,"E69.1");Q1=makeQuery(id+"F16.imprint","IMPRINT",FACE,{"disambiguationData":[TD([[makeQuery(id+"F16.imprint","IMPRINT",EDGE,{"derivedFrom":subQ4}),-1.0]])]});}
            var Q2;
            Q2=makeQuery(id+"F16.imprint","IMPRINT",FACE,{"disambiguationData":[TD([[makeQuery(id+"F16.imprint","IMPRINT",EDGE,{"derivedFrom":sQuery(id+"F16.wireOp",EDGE,"E68")}),1.0]])]});
            extrude(context, id + "F17", {"entities" : qUnion([Q0, Q1, Q2]), "operationType" : NewBodyOperationType.REMOVE, "oppositeDirection" : true, "depth" : 25 * mm});
        }
        {
            var Q0;
            Q0=qCreatedBy(makeId("Front.planeOp"),FACE);
            cPlane(context, id + "F18", {"entities" : qUnion([Q0]), "cplaneType" : CPlaneType.OFFSET, "offset" : 14 * mm, "oppositeDirection" : true, "width" : 150 * mm, "height" : 150 * mm});
        }
        {
            var Q0;
            Q0=qCreatedBy(id+"F18.planeOp",FACE);
            var sketch = newSketch(context, id + "F19", { "sketchPlane" : qUnion([Q0])});
            skLineSegment(sketch, "E78", {"start": v(4, 4) * mm, "end": v(4, 9.2) * mm});
            skLineSegment(sketch, "E79.bottom", {"start": v(3.6, 9.2) * mm, "end": v(-3.6, 9.2) * mm});
            skLineSegment(sketch, "E79.left", {"start": v(4, 8.8) * mm, "end": v(4, 4.4) * mm});
            skLineSegment(sketch, "E79.right", {"start": v(-4, 8.8) * mm, "end": v(-4, 4.4) * mm});
            skLineSegment(sketch, "E80", {"start": v(0, 0) * mm, "end": v(0, 4) * mm});
            skLineSegment(sketch, "E81", {"start": v(0, 4) * mm, "end": v(3.6, 4) * mm});
            skLineSegment(sketch, "E82", {"start": v(0, 4) * mm, "end": v(-3.6, 4) * mm});
            skPoint(sketch, "E83.orphan", {"position": v(-4, 0) * mm});
            skPoint(sketch, "E79.top.start.orphan", {"position": v(4, 0) * mm});
            skPoint(sketch, "E84.visualSharp", {"position": v(4, 4) * mm});
            skArc(sketch, "E84.filletArc", {"start": v(3.6, 4) * mm, "mid": v(3.88, 4.12) * mm, "end": v(4, 4.4) * mm});
            skPoint(sketch, "E85.visualSharp", {"position": v(-4, 4) * mm});
            skArc(sketch, "E85.filletArc", {"start": v(-4, 4.4) * mm, "mid": v(-3.88, 4.12) * mm, "end": v(-3.6, 4) * mm});
            skPoint(sketch, "E86.visualSharp", {"position": v(-4, 9.2) * mm});
            skArc(sketch, "E86.filletArc", {"start": v(-3.6, 9.2) * mm, "mid": v(-3.88, 9.08) * mm, "end": v(-4, 8.8) * mm});
            skPoint(sketch, "E87.visualSharp", {"position": v(4, 9.2) * mm});
            skArc(sketch, "E87.filletArc", {"start": v(4, 8.8) * mm, "mid": v(3.88, 9.08) * mm, "end": v(3.6, 9.2) * mm});
            skSolve(sketch);
        }
        {
            var Q0;
            Q0=qCreatedBy(makeId("Right.planeOp"),FACE);
            var sketch = newSketch(context, id + "F20", { "sketchPlane" : qUnion([Q0])});
            skLineSegment(sketch, "E88", {"start": v(0, 0) * mm, "end": v(14.4, 0) * mm});
            skLineSegment(sketch, "E89", {"start": v(14.4, 0) * mm, "end": v(14.4, 4) * mm});
            skLineSegment(sketch, "E90", {"start": v(14.4, 4) * mm, "end": v(26.4, 4) * mm});
            skLineSegment(sketch, "E91", {"start": v(26.4, 4) * mm, "end": v(35, 4) * mm});
            skLineSegment(sketch, "E92", {"start": v(35, 4) * mm, "end": v(35, 9.6) * mm});
            skFitSpline(sketch, "E93", {"points": [v(26.4, 4) * mm, v(30.4, 4.73) * mm, v(32.04, 5.93) * mm, v(33.82, 8.02) * mm, v(35, 9.6) * mm], "startDerivative": vector(21.55, 0) * mm, "endDerivative": vector(8.23, 6.38) * mm});
            skLineSegment(sketch, "E94", {"start": v(35, 9.6) * mm, "end": v(36.63, 9.93) * mm});
            skSolve(sketch);
        }
        {
            var Q0;
            Q0=makeQuery(id+"F19.imprint","IMPRINT",FACE,{"disambiguationData":[TD([[makeQuery(id+"F19.imprint","IMPRINT",EDGE,{"derivedFrom":sQuery(id+"F19.wireOp",EDGE,"E79.bottom")}),1.0]])]});
            var Q1;
            Q1=sQuery(id+"F20.wireOp",EDGE,"E93");
            var Q2;
            Q2=sQuery(id+"F20.wireOp",EDGE,"E90");
            var Q3;
            Q3=sQuery(id+"F20.wireOp",EDGE,"E94");
            sweep(context, id + "F21", {"operationType" : NewBodyOperationType.REMOVE, "profiles" : qUnion([Q0]), "path" : qUnion([Q1, Q2, Q3])});
        }
        {
            var Q0;
            Q0=qCreatedBy(id+"F13.planeOp",FACE);
            var sketch = newSketch(context, id + "F22", { "sketchPlane" : qUnion([Q0])});
            skLineSegment(sketch, "E95", {"start": v(0, 0) * mm, "end": v(0, 37.45) * mm});
            skLineSegment(sketch, "E96", {"start": v(-11.35, 37.45) * mm, "end": v(0, 37.45) * mm});
            skPoint(sketch, "E97.visualSharp", {"position": v(-11.35, 45.75) * mm});
            skLineSegment(sketch, "E98.MirrorCS", {"start": v(11.35, 37.45) * mm, "end": v(0, 37.45) * mm});
            skPoint(sketch, "E99.MirrorP", {"position": v(11.35, 45.75) * mm});
            skLineSegment(sketch, "E100", {"start": v(1.4, 39.6) * mm, "end": v(3.52, 41.66) * mm});
            skLineSegment(sketch, "E101", {"start": v(0.04, 50.25) * mm, "end": v(0, 50.25) * mm});
            skLineSegment(sketch, "E102", {"start": v(0, 50.25) * mm, "end": v(0, 52.25) * mm});
            skPoint(sketch, "E103.visualSharp", {"position": v(12.4, 52.25) * mm});
            skPoint(sketch, "E104.visualSharp", {"position": v(12.4, 50.25) * mm});
            skArc(sketch, "E104.filletArc", {"start": v(3.52, 41.66) * mm, "mid": v(4.68, 47.13) * mm, "end": v(0.04, 50.25) * mm});
            skLineSegment(sketch, "E105.MirrorCS", {"start": v(-0.04, 50.25) * mm, "end": v(0, 50.25) * mm});
            skArc(sketch, "E106.MirrorCS", {"start": v(-3.52, 41.66) * mm, "mid": v(-4.68, 47.13) * mm, "end": v(-0.04, 50.25) * mm});
            skLineSegment(sketch, "E107.MirrorCS", {"start": v(-1.4, 39.6) * mm, "end": v(-3.52, 41.66) * mm});
            skPoint(sketch, "E108.visualSharp", {"position": v(0, 38.25) * mm});
            skArc(sketch, "E108.filletArc", {"start": v(-1.4, 39.6) * mm, "mid": v(0, 39.03) * mm, "end": v(1.4, 39.6) * mm});
            skLineSegment(sketch, "E109", {"start": v(-11.2, 26.25) * mm, "end": v(-4.2, 26.25) * mm});
            skLineSegment(sketch, "E110", {"start": v(-4.2, 26.25) * mm, "end": v(-4.2, 30.84) * mm});
            skLineSegment(sketch, "E111", {"start": v(-5.9, 31.54) * mm, "end": v(-10.5, 26.96) * mm});
            skLineSegment(sketch, "E112.MirrorCS", {"start": v(-4.2, 26.25) * mm, "end": v(-4.2, 21.66) * mm});
            skLineSegment(sketch, "E113.MirrorCS", {"start": v(-5.9, 20.96) * mm, "end": v(-10.5, 25.54) * mm});
            skPoint(sketch, "E114.visualSharp", {"position": v(-4.2, 33.25) * mm});
            skArc(sketch, "E114.filletArc", {"start": v(-4.2, 30.84) * mm, "mid": v(-4.82, 31.76) * mm, "end": v(-5.9, 31.54) * mm});
            skPoint(sketch, "E115.visualSharp", {"position": v(-4.2, 19.25) * mm});
            skArc(sketch, "E115.filletArc", {"start": v(-5.9, 20.96) * mm, "mid": v(-4.82, 20.74) * mm, "end": v(-4.2, 21.66) * mm});
            skPoint(sketch, "E116.visualSharp", {"position": v(-11.2, 26.25) * mm});
            skArc(sketch, "E116.filletArc", {"start": v(-10.5, 26.96) * mm, "mid": v(-10.79, 26.25) * mm, "end": v(-10.5, 25.54) * mm});
            skLineSegment(sketch, "E117.MirrorCS", {"start": v(11.2, 26.25) * mm, "end": v(4.2, 26.25) * mm});
            skLineSegment(sketch, "E118.MirrorCS", {"start": v(5.9, 31.54) * mm, "end": v(10.5, 26.96) * mm});
            skArc(sketch, "E119.MirrorCS", {"start": v(10.5, 26.96) * mm, "mid": v(10.79, 26.25) * mm, "end": v(10.5, 25.54) * mm});
            skLineSegment(sketch, "E120.MirrorCS", {"start": v(4.2, 26.25) * mm, "end": v(4.2, 30.84) * mm});
            skArc(sketch, "E121.MirrorCS", {"start": v(4.2, 30.84) * mm, "mid": v(4.82, 31.76) * mm, "end": v(5.9, 31.54) * mm});
            skPoint(sketch, "E122.MirrorP", {"position": v(4.2, 19.25) * mm});
            skArc(sketch, "E123.MirrorCS", {"start": v(5.9, 20.96) * mm, "mid": v(4.82, 20.74) * mm, "end": v(4.2, 21.66) * mm});
            skLineSegment(sketch, "E124.MirrorCS", {"start": v(5.9, 20.96) * mm, "end": v(10.5, 25.54) * mm});
            skLineSegment(sketch, "E125.MirrorCS", {"start": v(4.2, 26.25) * mm, "end": v(4.2, 21.66) * mm});
            skPoint(sketch, "E126.MirrorP", {"position": v(11.2, 26.25) * mm});
            skCircle(sketch, "E127", {"center": v(8.02, 37.45) * mm, "radius": 3.33 * mm});
            skCircle(sketch, "E128.MirrorC", {"center": v(-8.02, 37.45) * mm, "radius": 3.33 * mm});
            skCircle(sketch, "E129", {"center": v(8.74, 17.27) * mm, "radius": 2.2 * mm});
            skCircle(sketch, "E130.MirrorC", {"center": v(-8.74, 17.27) * mm, "radius": 2.2 * mm});
            skCircle(sketch, "E131", {"center": v(6.74, 58.56) * mm, "radius": 3.25 * mm});
            skLineSegment(sketch, "E132", {"start": v(0, 55.31) * mm, "end": v(6.74, 55.31) * mm});
            skCircle(sketch, "E133.MirrorC", {"center": v(-6.74, 58.56) * mm, "radius": 3.25 * mm});
            skLineSegment(sketch, "E134", {"start": v(9.04, 60.86) * mm, "end": v(7.44, 62.45) * mm});
            skLineSegment(sketch, "E135", {"start": v(6.03, 62.45) * mm, "end": v(4.44, 60.86) * mm});
            skPoint(sketch, "E136.visualSharp", {"position": v(6.74, 63.16) * mm});
            skArc(sketch, "E136.filletArc", {"start": v(7.44, 62.45) * mm, "mid": v(6.74, 62.74) * mm, "end": v(6.03, 62.45) * mm});
            skLineSegment(sketch, "E137.MirrorCS", {"start": v(-6.03, 62.45) * mm, "end": v(-4.44, 60.86) * mm});
            skLineSegment(sketch, "E138.MirrorCS", {"start": v(-9.04, 60.86) * mm, "end": v(-7.44, 62.45) * mm});
            skArc(sketch, "E139.MirrorCS", {"start": v(-7.44, 62.45) * mm, "mid": v(-6.74, 62.74) * mm, "end": v(-6.03, 62.45) * mm});
            skCircle(sketch, "E140", {"center": v(0, 34.46) * mm, "radius": 2.97 * mm});
            skSolve(sketch);
        }
        {
            var Q0;
            Q0=qSketchRegion(id+"F22",true);
            var Q1;
            {var subQ0=sQuery(id+"F1.wireOp",EDGE,"E37.MirrorCS");var subQ1=makeQuery(id+"F2.opExtrude","SWEPT_FACE",FACE,{"disambiguationData":[OSD([subQ0])]});var subQ2=sQuery(id+"F1.wireOp",EDGE,"E36.MirrorCS");var subQ3=sQuery(id+"F1.wireOp",EDGE,"E35");var subQ4=sQuery(id+"F1.wireOp",EDGE,"E38.MirrorCS");Q1=makeQuery(id+"F8.boolean.opBoolean","SPLIT",FACE,{"disambiguationData":[TD([makeQuery(id+"F2.opExtrude","CAP_FACE",FACE,{"disambiguationData":[OSD([sQuery(id+"F1.wireOp",EDGE,"E24"),sQuery(id+"F1.wireOp",EDGE,"E25"),sQuery(id+"F1.wireOp",EDGE,"E31"),sQuery(id+"F1.wireOp",EDGE,"E32"),sQuery(id+"F1.wireOp",EDGE,"E33"),sQuery(id+"F1.wireOp",EDGE,"E34"),subQ3,subQ2,subQ0,subQ4])],"isStart":true})])],"derivedFrom":subQ1});}
            extrude(context, id + "F23", {"entities" : qUnion([Q0]), "operationType" : NewBodyOperationType.REMOVE, "endBound" : BoundingType.UP_TO_SURFACE, "endBoundEntityFace" : qUnion([Q1]), "depth" : 8 * mm});
        }
        {
            var Q0;
            Q0=makeQuery(id+"F8.boolean.opBoolean","MERGE",FACE,{"derivedFrom":[makeQuery(id+"F2.opExtrude","SWEPT_FACE",FACE,{"disambiguationData":[OSD([sQuery(id+"F1.wireOp",EDGE,"E24"),sQuery(id+"F1.wireOp",EDGE,"E25")])]}),makeQuery(id+"F8.opExtrude","CAP_FACE",FACE,{"disambiguationData":[OSD([sQuery(id+"F7.wireOp",EDGE,"E41"),sQuery(id+"F7.wireOp",EDGE,"E42"),sQuery(id+"F7.wireOp",EDGE,"E44"),sQuery(id+"F7.wireOp",EDGE,"E45.MirrorCS"),sQuery(id+"F7.wireOp",EDGE,"E46.MirrorCS"),sQuery(id+"F7.wireOp",EDGE,"E47.MirrorCS"),sQuery(id+"F7.wireOp",EDGE,"E48.trimOffspring")])],"isStart":true})]});
            var sketch = newSketch(context, id + "F24", { "sketchPlane" : qUnion([Q0])});
            skLineSegment(sketch, "E141", {"start": v(11.35, -16.5) * mm, "end": v(11.35, -9.42) * mm});
            skLineSegment(sketch, "E142.MirrorCS", {"start": v(-11.35, -16.5) * mm, "end": v(-11.35, -9.42) * mm});
            skLineSegment(sketch, "E143", {"start": v(11.35, -16.5) * mm, "end": v(11.35, -12.6) * mm});
            skLineSegment(sketch, "E144", {"start": v(15.25, -4.5) * mm, "end": v(15.25, -12.6) * mm});
            skLineSegment(sketch, "E145.MirrorCS", {"start": v(-15.25, -4.5) * mm, "end": v(-15.25, -12.6) * mm});
            skLineSegment(sketch, "E146", {"start": v(11.35, -12.6) * mm, "end": v(11.35, -9.42) * mm});
            skLineSegment(sketch, "E147", {"start": v(11.35, -16.5) * mm, "end": v(15.25, -12.6) * mm});
            skLineSegment(sketch, "E148", {"start": v(-11.35, -16.5) * mm, "end": v(-15.25, -12.6) * mm});
            skLineSegment(sketch, "E149", {"start": v(11.35, -10.22) * mm, "end": v(15.25, -4.5) * mm});
            skLineSegment(sketch, "E150.MirrorCS", {"start": v(-11.35, -10.22) * mm, "end": v(-15.25, -4.5) * mm});
            skPoint(sketch, "E151.MirrorCS.end.orphan", {"position": v(-15.25, -4.5) * mm});
            skSolve(sketch);
        }
        {
            var Q0;
            Q0=qSketchRegion(id+"F24",true);
            var Q1;
            {var subQ0=sQuery(id+"F1.wireOp",EDGE,"E38.MirrorCS");var subQ1=sQuery(id+"F1.wireOp",EDGE,"E37.MirrorCS");var subQ2=sQuery(id+"F1.wireOp",EDGE,"E36.MirrorCS");var subQ3=sQuery(id+"F1.wireOp",EDGE,"E35");var subQ4=sQuery(id+"F1.wireOp",EDGE,"E34");var subQ5=sQuery(id+"F1.wireOp",EDGE,"E33");var subQ6=sQuery(id+"F1.wireOp",EDGE,"E32");var subQ7=sQuery(id+"F1.wireOp",EDGE,"E31");var subQ8=sQuery(id+"F1.wireOp",EDGE,"E25");var subQ9=sQuery(id+"F1.wireOp",EDGE,"E24");var subQ13=makeQuery(id+"F2.opExtrude","SWEPT_FACE",FACE,{"disambiguationData":[OSD([subQ3,subQ2])]});Q1=makeQuery(id+"F8.boolean.opBoolean","MERGE",FACE,{"derivedFrom":[makeQuery(id+"F5.boolean.opBoolean","SPLIT",FACE,{"disambiguationData":[TD([makeQuery(id+"F2.opExtrude","CAP_FACE",FACE,{"disambiguationData":[OSD([subQ9,subQ8,subQ7,subQ6,subQ5,subQ4,subQ3,subQ2,subQ1,subQ0])],"isStart":true})])],"derivedFrom":subQ13}),makeQuery(id+"F5.boolean.opBoolean","SPLIT",FACE,{"disambiguationData":[TD([makeQuery(id+"F2.opExtrude","CAP_FACE",FACE,{"disambiguationData":[OSD([subQ9,subQ8,subQ7,subQ6,subQ5,subQ4,subQ3,subQ2,subQ1,subQ0])],"isStart":false})])],"derivedFrom":subQ13}),makeQuery(id+"F8.opExtrude","CAP_FACE",FACE,{"disambiguationData":[OSD([sQuery(id+"F7.wireOp",EDGE,"E41"),sQuery(id+"F7.wireOp",EDGE,"E42"),sQuery(id+"F7.wireOp",EDGE,"E44"),sQuery(id+"F7.wireOp",EDGE,"E45.MirrorCS"),sQuery(id+"F7.wireOp",EDGE,"E46.MirrorCS"),sQuery(id+"F7.wireOp",EDGE,"E47.MirrorCS"),sQuery(id+"F7.wireOp",EDGE,"E48.trimOffspring")])],"isStart":false})]});}
            extrude(context, id + "F25", {"entities" : qUnion([Q0]), "operationType" : NewBodyOperationType.ADD, "endBound" : BoundingType.UP_TO_SURFACE, "oppositeDirection" : true, "endBoundEntityFace" : qUnion([Q1]), "depth" : 25 * mm});
        }
        {
            var Q0;
            Q0=makeQuery(id+"F5.boolean.opBoolean","COPY",EDGE,{"derivedFrom":makeQuery(id+"F5.opExtrude","CAP_EDGE",EDGE,{"disambiguationData":[OSD([sQuery(id+"F4.wireOp",EDGE,"E39")])],"isStart":false})});
            fillet(context, id + "F26", {"entities" : qUnion([Q0]), "radius" : 1.5 * mm, "tangentPropagation" : true, "allowEdgeOverflow" : false});
        }
        {
            var Q0;
            Q0=makeQuery(id+"F12.boolean.opBoolean","COPY",EDGE,{"derivedFrom":makeQuery(id+"F12.opExtrude","CAP_EDGE",EDGE,{"disambiguationData":[OSD([sQuery(id+"F11.wireOp",EDGE,"E59.MirrorC")])],"isStart":false})});
            var Q1;
            Q1=makeQuery(id+"F12.boolean.opBoolean","COPY",EDGE,{"derivedFrom":makeQuery(id+"F12.opExtrude","CAP_EDGE",EDGE,{"disambiguationData":[OSD([sQuery(id+"F11.wireOp",EDGE,"E54")])],"isStart":false})});
            var Q2;
            Q2=makeQuery(id+"F12.boolean.opBoolean","COPY",EDGE,{"derivedFrom":makeQuery(id+"F12.opExtrude","CAP_EDGE",EDGE,{"disambiguationData":[OSD([sQuery(id+"F11.wireOp",EDGE,"E58")])],"isStart":false})});
            var Q3;
            Q3=makeQuery(id+"F12.boolean.opBoolean","COPY",EDGE,{"derivedFrom":makeQuery(id+"F12.opExtrude","CAP_EDGE",EDGE,{"disambiguationData":[OSD([sQuery(id+"F11.wireOp",EDGE,"E56")])],"isStart":false})});
            fillet(context, id + "F27", {"entities" : qUnion([Q0, Q1, Q2, Q3]), "radius" : .4 * mm, "tangentPropagation" : true, "allowEdgeOverflow" : false});
        }
    });
